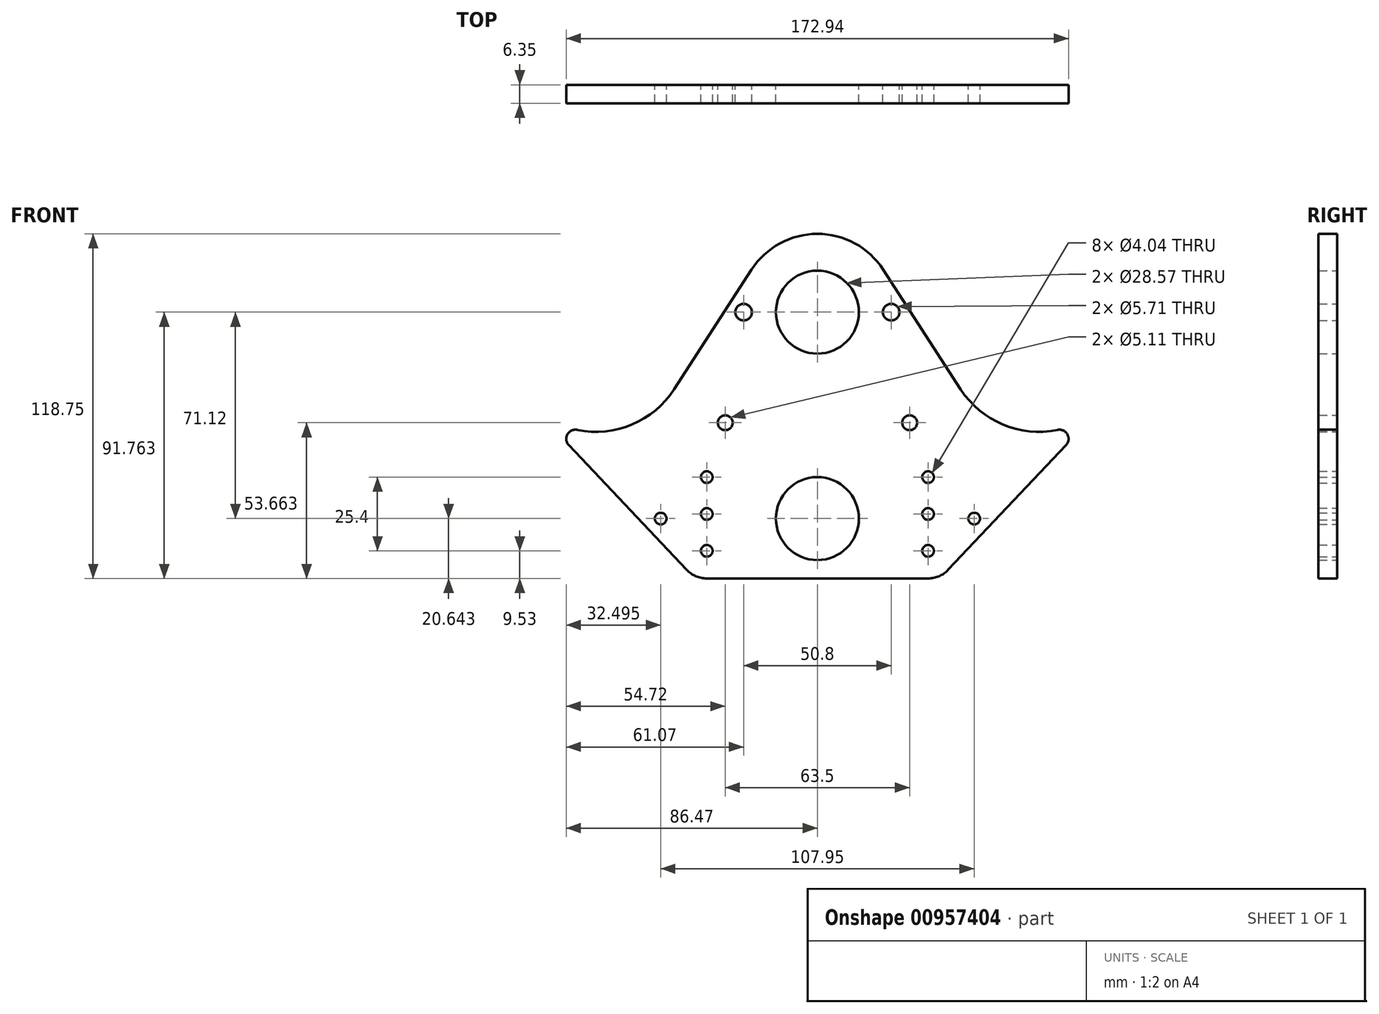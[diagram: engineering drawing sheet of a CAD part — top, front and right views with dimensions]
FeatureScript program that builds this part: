
annotation { "Feature Type Name" : "Feature", "Feature Type Description" : "" }
export const myFeature = defineFeature(function(context is Context, id is Id, definition is map)
    precondition{}
    {
        {
            var Q0;
            Q0=qCreatedBy(makeId("Front.planeOp"),FACE);
            var sketch = newSketch(context, id + "F0", { "sketchPlane" : qUnion([Q0])});
            skCircle(sketch, "E0", {"center": v(-76.2, 60.32) * mm, "radius": 32 * mm, "construction": true});
            skCircle(sketch, "E1", {"center": v(76.2, 60.33) * mm, "radius": 32 * mm, "construction": true});
            skLineSegment(sketch, "E2", {"start": v(-76.2, 60.33) * mm, "end": v(76.2, 60.33) * mm, "construction": true});
            skLineSegment(sketch, "E3", {"start": v(0, 60.33) * mm, "end": v(0, 0) * mm, "construction": true});
            skLineSegment(sketch, "E4.bottom", {"start": v(-127, 25.4) * mm, "end": v(127, 25.4) * mm, "construction": true});
            skLineSegment(sketch, "E4.top", {"start": v(-127, -25.4) * mm, "end": v(127, -25.4) * mm, "construction": true});
            skLineSegment(sketch, "E4.left", {"start": v(-127, 25.4) * mm, "end": v(-127, -25.4) * mm, "construction": true});
            skLineSegment(sketch, "E4.right", {"start": v(127, 25.4) * mm, "end": v(127, -25.4) * mm, "construction": true});
            skPoint(sketch, "E4.middle", {"position": v(0, 0) * mm});
            skCircle(sketch, "E5", {"center": v(0, 69.53) * mm, "radius": 34.3 * mm, "construction": true});
            skCircle(sketch, "E6", {"center": v(0, 69.53) * mm, "radius": 26.99 * mm, "construction": true});
            skCircle(sketch, "E7", {"center": v(0, 69.53) * mm, "radius": 38.1 * mm, "construction": true});
            skCircle(sketch, "E8", {"center": v(0, -1.59) * mm, "radius": 33.02 * mm, "construction": true});
            skCircle(sketch, "E9", {"center": v(0, -1.59) * mm, "radius": 44.13 * mm, "construction": true});
            skCircle(sketch, "E10", {"center": v(0, 69.53) * mm, "radius": 14.29 * mm});
            skCircle(sketch, "E11", {"center": v(0, -1.59) * mm, "radius": 14.29 * mm});
            skCircle(sketch, "E12", {"center": v(-38.1, 12.7) * mm, "radius": 9.53 * mm, "construction": true});
            skCircle(sketch, "E13", {"center": v(-38.1, -12.7) * mm, "radius": 9.53 * mm, "construction": true});
            skCircle(sketch, "E14", {"center": v(38.1, -12.7) * mm, "radius": 9.53 * mm, "construction": true});
            skCircle(sketch, "E15", {"center": v(38.1, 12.7) * mm, "radius": 9.53 * mm, "construction": true});
            skCircle(sketch, "E16", {"center": v(38.1, 0) * mm, "radius": 9.53 * mm, "construction": true});
            skCircle(sketch, "E17", {"center": v(-38.1, 0) * mm, "radius": 9.53 * mm, "construction": true});
            skCircle(sketch, "E18", {"center": v(38.1, -12.7) * mm, "radius": 2.02 * mm});
            skCircle(sketch, "E19", {"center": v(38.1, 0) * mm, "radius": 2.02 * mm});
            skCircle(sketch, "E20", {"center": v(38.1, 12.7) * mm, "radius": 2.02 * mm});
            skCircle(sketch, "E21", {"center": v(-38.1, 12.7) * mm, "radius": 2.02 * mm});
            skCircle(sketch, "E22", {"center": v(-38.1, 0) * mm, "radius": 2.02 * mm});
            skCircle(sketch, "E23", {"center": v(-38.1, -12.7) * mm, "radius": 2.02 * mm});
            skArc(sketch, "E24", {"start": v(-82.66, 28.98) * mm, "mid": v(-63.83, 30.8) * mm, "end": v(-49.32, 42.95) * mm});
            skLineSegment(sketch, "E25", {"start": v(-85.6, 23.69) * mm, "end": v(-45.02, -19.24) * mm});
            skPoint(sketch, "E26.visualSharp", {"position": v(-99.46, 38.34) * mm});
            skArc(sketch, "E26.filletArc", {"start": v(-82.66, 28.98) * mm, "mid": v(-86.07, 27.42) * mm, "end": v(-85.6, 23.69) * mm});
            skLineSegment(sketch, "E27", {"start": v(-49.32, 42.95) * mm, "end": v(-22.66, 84.19) * mm});
            skArc(sketch, "E28", {"start": v(-22.66, 84.19) * mm, "mid": v(0, 96.52) * mm, "end": v(22.66, 84.19) * mm});
            skLineSegment(sketch, "E29", {"start": v(22.66, 84.19) * mm, "end": v(49.32, 42.95) * mm});
            skArc(sketch, "E30", {"start": v(49.32, 42.95) * mm, "mid": v(63.83, 30.8) * mm, "end": v(82.66, 28.98) * mm});
            skLineSegment(sketch, "E31", {"start": v(85.6, 23.69) * mm, "end": v(45.02, -19.24) * mm});
            skArc(sketch, "E32", {"start": v(-45.02, -19.24) * mm, "mid": v(-41.87, -21.45) * mm, "end": v(-38.1, -22.22) * mm});
            skArc(sketch, "E33", {"start": v(45.02, -19.24) * mm, "mid": v(41.87, -21.45) * mm, "end": v(38.1, -22.22) * mm});
            skLineSegment(sketch, "E34", {"start": v(38.1, -22.22) * mm, "end": v(-38.1, -22.23) * mm});
            skPoint(sketch, "E35.visualSharp", {"position": v(99.46, 38.34) * mm});
            skArc(sketch, "E35.filletArc", {"start": v(85.6, 23.69) * mm, "mid": v(86.07, 27.42) * mm, "end": v(82.66, 28.98) * mm});
            skLineSegment(sketch, "E36.bottom", {"start": v(-38.1, 12.7) * mm, "end": v(38.1, 12.7) * mm, "construction": true});
            skLineSegment(sketch, "E36.top", {"start": v(-38.1, -12.7) * mm, "end": v(38.1, -12.7) * mm, "construction": true});
            skLineSegment(sketch, "E36.left", {"start": v(-38.1, 12.7) * mm, "end": v(-38.1, -12.7) * mm, "construction": true});
            skLineSegment(sketch, "E36.right", {"start": v(38.1, 12.7) * mm, "end": v(38.1, -12.7) * mm, "construction": true});
            skLineSegment(sketch, "E37", {"start": v(-25.4, 69.53) * mm, "end": v(0, 69.53) * mm, "construction": true});
            skLineSegment(sketch, "E38", {"start": v(0, 69.53) * mm, "end": v(25.4, 69.53) * mm, "construction": true});
            skCircle(sketch, "E39", {"center": v(-25.4, 69.53) * mm, "radius": 4.76 * mm, "construction": true});
            skCircle(sketch, "E40", {"center": v(25.4, 69.53) * mm, "radius": 4.76 * mm, "construction": true});
            skCircle(sketch, "E41", {"center": v(-25.4, 69.53) * mm, "radius": 2.86 * mm});
            skCircle(sketch, "E42", {"center": v(25.4, 69.53) * mm, "radius": 2.86 * mm});
            skCircle(sketch, "E43", {"center": v(31.75, 31.43) * mm, "radius": 6.35 * mm, "construction": true});
            skCircle(sketch, "E44", {"center": v(31.75, 31.43) * mm, "radius": 2.55 * mm});
            skCircle(sketch, "E45.MirrorC", {"center": v(-31.75, 31.43) * mm, "radius": 6.35 * mm, "construction": true});
            skCircle(sketch, "E46.MirrorC", {"center": v(-31.75, 31.43) * mm, "radius": 2.55 * mm});
            skLineSegment(sketch, "E47", {"start": v(-38.1, 12.7) * mm, "end": v(38.1, -12.7) * mm, "construction": true});
            skCircle(sketch, "E48", {"center": v(0, -1.59) * mm, "radius": 50.8 * mm, "construction": true});
            skLineSegment(sketch, "E49", {"start": v(-31.75, 31.43) * mm, "end": v(31.75, 31.43) * mm, "construction": true});
            skLineSegment(sketch, "E50", {"start": v(-53.98, -1.59) * mm, "end": v(0, -1.59) * mm, "construction": true});
            skLineSegment(sketch, "E51", {"start": v(0, -1.59) * mm, "end": v(53.98, -1.59) * mm, "construction": true});
            skCircle(sketch, "E52", {"center": v(53.98, -1.59) * mm, "radius": 2.02 * mm});
            skCircle(sketch, "E53", {"center": v(-53.98, -1.59) * mm, "radius": 2.02 * mm});
            skCircle(sketch, "E54", {"center": v(53.98, -1.59) * mm, "radius": 9.53 * mm, "construction": true});
            skCircle(sketch, "E55", {"center": v(-53.98, -1.59) * mm, "radius": 9.53 * mm, "construction": true});
            skSolve(sketch);
        }
        {
            var Q0;
            Q0=qSketchRegion(id+"F0",true);
            extrude(context, id + "F1", {"entities" : qUnion([Q0]), "depth" : 6.35 * mm, "offsetDistance" : 25.4 * mm});
        }
    });
